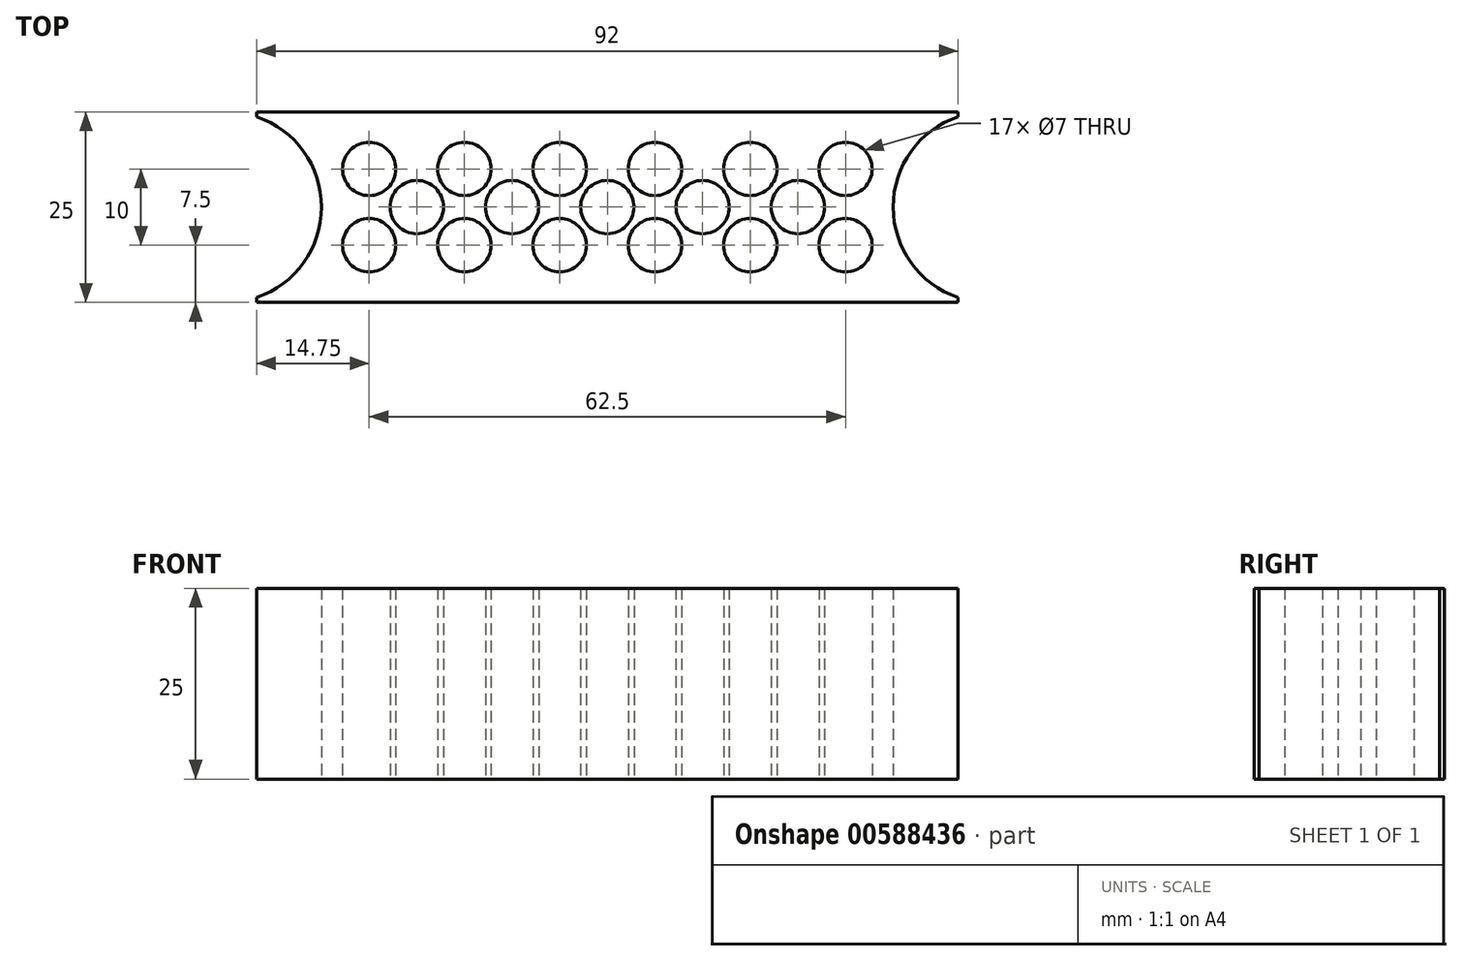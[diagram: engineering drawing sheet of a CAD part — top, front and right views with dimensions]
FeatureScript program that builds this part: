
annotation { "Feature Type Name" : "Feature", "Feature Type Description" : "" }
export const myFeature = defineFeature(function(context is Context, id is Id, definition is map)
    precondition{}
    {
        {
            var Q0;
            Q0=qCreatedBy(makeId("Top.planeOp"),FACE);
            var sketch = newSketch(context, id + "F0", { "sketchPlane" : qUnion([Q0])});
            skLineSegment(sketch, "E0.bottom", {"start": v(50, 12.5) * mm, "end": v(-50, 12.5) * mm});
            skLineSegment(sketch, "E0.top", {"start": v(50, -12.5) * mm, "end": v(-50, -12.5) * mm});
            skLineSegment(sketch, "E0.left", {"start": v(50, 12.5) * mm, "end": v(50, -12.5) * mm});
            skLineSegment(sketch, "E0.right", {"start": v(-50, 12.5) * mm, "end": v(-50, -12.5) * mm});
            skPoint(sketch, "E0.middle", {"position": v(0, 0) * mm});
            skCircle(sketch, "E1", {"center": v(50, 0) * mm, "radius": 12.5 * mm});
            skCircle(sketch, "E2", {"center": v(-50, 0) * mm, "radius": 12.5 * mm});
            skLineSegment(sketch, "E3", {"start": v(-46, 12.5) * mm, "end": v(-46, -12.5) * mm});
            skLineSegment(sketch, "E4", {"start": v(46, 12.5) * mm, "end": v(46, -12.5) * mm});
            skPoint(sketch, "E5.startSnap0", {"position": v(31.25, 5) * mm});
            skPoint(sketch, "E6.startSnap0", {"position": v(-31.25, 5) * mm});
            skCircle(sketch, "E7", {"center": v(-31.25, 5) * mm, "radius": 3.5 * mm});
            skCircle(sketch, "E8", {"center": v(-31.25, -5) * mm, "radius": 3.5 * mm});
            skCircle(sketch, "E9", {"center": v(-18.75, 5) * mm, "radius": 3.5 * mm});
            skCircle(sketch, "E10", {"center": v(-18.75, -5) * mm, "radius": 3.5 * mm});
            skCircle(sketch, "E11", {"center": v(-25, 0) * mm, "radius": 3.5 * mm});
            skCircle(sketch, "E12", {"center": v(-12.5, 0) * mm, "radius": 3.5 * mm});
            skCircle(sketch, "E13", {"center": v(0, 0) * mm, "radius": 3.5 * mm});
            skCircle(sketch, "E14", {"center": v(25, 0) * mm, "radius": 3.5 * mm});
            skCircle(sketch, "E15", {"center": v(12.5, 0) * mm, "radius": 3.5 * mm});
            skCircle(sketch, "E16", {"center": v(18.75, 5) * mm, "radius": 3.5 * mm});
            skCircle(sketch, "E17", {"center": v(6.25, 5) * mm, "radius": 3.5 * mm});
            skCircle(sketch, "E18", {"center": v(6.25, -5) * mm, "radius": 3.5 * mm});
            skCircle(sketch, "E19", {"center": v(31.25, -5) * mm, "radius": 3.5 * mm});
            skCircle(sketch, "E20", {"center": v(31.25, 5) * mm, "radius": 3.5 * mm});
            skCircle(sketch, "E21", {"center": v(18.75, -5) * mm, "radius": 3.5 * mm});
            skCircle(sketch, "E22", {"center": v(-6.25, 5) * mm, "radius": 3.5 * mm});
            skCircle(sketch, "E23", {"center": v(-6.25, -5) * mm, "radius": 3.5 * mm});
            skSolve(sketch);
        }
        {
            var Q0;
            Q0=makeQuery(id+"F0.imprint","IMPRINT",FACE,{"disambiguationData":[TD([[makeQuery(id+"F0.imprint","IMPRINT",EDGE,{"derivedFrom":sQuery(id+"F0.wireOp",EDGE,"E7")}),-1.0]])]});
            extrude(context, id + "F1", {"entities" : qUnion([Q0]), "depth" : 25 * mm, "offsetDistance" : 25 * mm});
        }
    });
